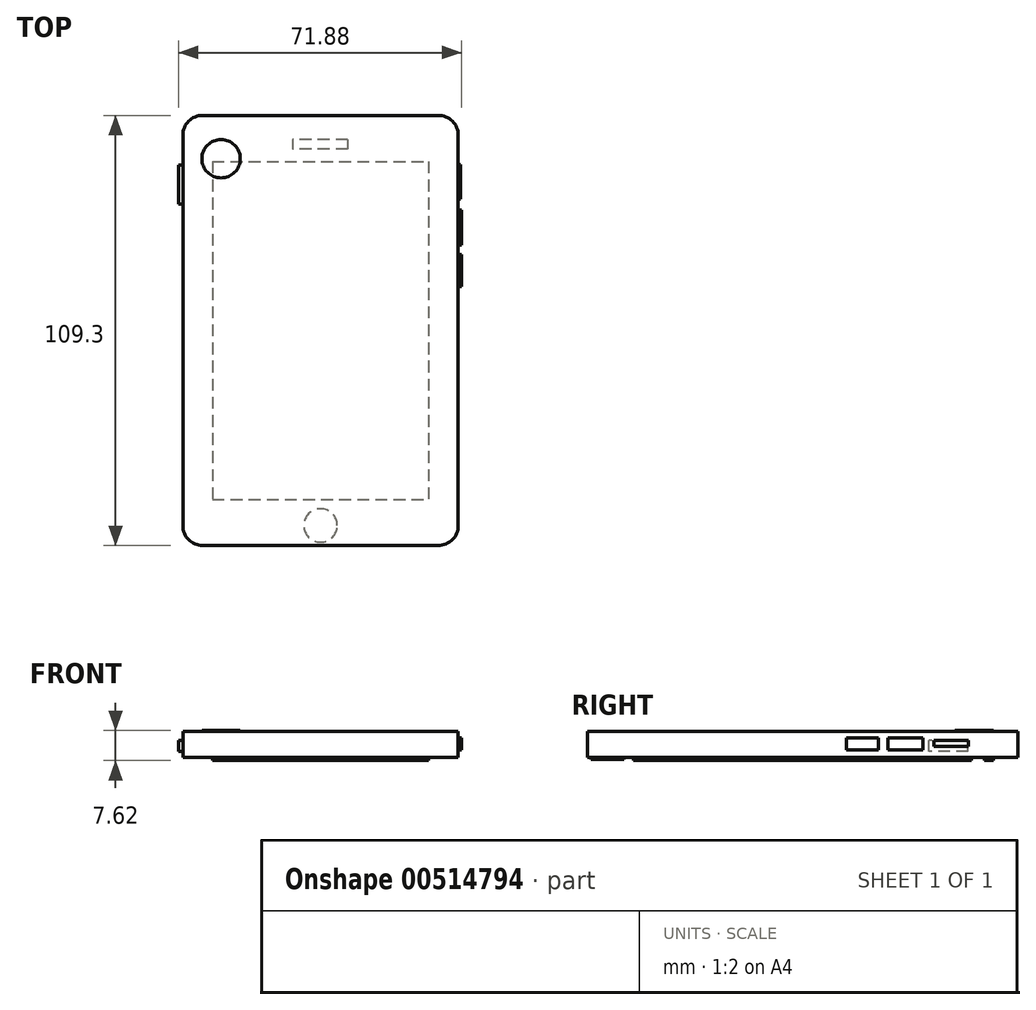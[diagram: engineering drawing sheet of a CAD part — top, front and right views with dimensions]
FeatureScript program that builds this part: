
annotation { "Feature Type Name" : "Feature", "Feature Type Description" : "" }
export const myFeature = defineFeature(function(context is Context, id is Id, definition is map)
    precondition{}
    {
        {
            var Q0;
            Q0=qCreatedBy(makeId("Top.planeOp"),FACE);
            var sketch = newSketch(context, id + "F0", { "sketchPlane" : qUnion([Q0])});
            skLineSegment(sketch, "E0.bottom", {"start": v(-30.02, 51.45) * mm, "end": v(30.02, 51.45) * mm});
            skLineSegment(sketch, "E0.top", {"start": v(-30.02, -51.45) * mm, "end": v(30.02, -51.45) * mm});
            skLineSegment(sketch, "E0.left", {"start": v(-30.02, 51.45) * mm, "end": v(-30.02, -51.45) * mm});
            skLineSegment(sketch, "E0.right", {"start": v(30.02, 51.45) * mm, "end": v(30.02, -51.45) * mm});
            skPoint(sketch, "E0.middle", {"position": v(0, 0) * mm});
            skLineSegment(sketch, "E1.bottom", {"start": v(-34.98, 54.65) * mm, "end": v(34.98, 54.65) * mm});
            skLineSegment(sketch, "E1.top", {"start": v(-34.98, -54.65) * mm, "end": v(34.98, -54.65) * mm});
            skLineSegment(sketch, "E1.left", {"start": v(-34.98, 54.65) * mm, "end": v(-34.98, -54.65) * mm});
            skLineSegment(sketch, "E1.right", {"start": v(34.98, 54.65) * mm, "end": v(34.98, -54.65) * mm});
            skSolve(sketch);
        }
        {
            var Q0;
            Q0=makeQuery(id+"F0.imprint","IMPRINT",FACE,{"disambiguationData":[TD([[makeQuery(id+"F0.imprint","IMPRINT",EDGE,{"derivedFrom":sQuery(id+"F0.wireOp",EDGE,"E0.bottom")}),-1.0]])]});
            var Q1;
            Q1=makeQuery(id+"F0.imprint","IMPRINT",FACE,{"disambiguationData":[TD([[makeQuery(id+"F0.imprint","IMPRINT",EDGE,{"derivedFrom":sQuery(id+"F0.wireOp",EDGE,"E0.bottom")}),1.0]])]});
            extrude(context, id + "F1", {"entities" : qUnion([Q0, Q1]), "depth" : 6.6 * mm, "offsetDistance" : 25.4 * mm});
        }
        {
            var Q0;
            Q0=makeQuery(id+"F1.opExtrude","SWEPT_EDGE",EDGE,{"disambiguationData":[OSD([sQuery(id+"F0.wireOp",EDGE,"E1.top"),sQuery(id+"F0.wireOp",EDGE,"E1.right")])]});
            fillet(context, id + "F2", {"entities" : qUnion([Q0]), "radius" : 5.08 * mm, "tangentPropagation" : true, "allowEdgeOverflow" : false});
        }
        {
            var Q0;
            Q0=makeQuery(id+"F1.opExtrude","SWEPT_EDGE",EDGE,{"disambiguationData":[OSD([sQuery(id+"F0.wireOp",EDGE,"E1.top"),sQuery(id+"F0.wireOp",EDGE,"E1.left")])]});
            fillet(context, id + "F3", {"entities" : qUnion([Q0]), "radius" : 5.08 * mm, "tangentPropagation" : true, "allowEdgeOverflow" : false});
        }
        {
            var Q0;
            Q0=makeQuery(id+"F1.opExtrude","SWEPT_EDGE",EDGE,{"disambiguationData":[OSD([sQuery(id+"F0.wireOp",EDGE,"E1.bottom"),sQuery(id+"F0.wireOp",EDGE,"E1.right")])]});
            fillet(context, id + "F4", {"entities" : qUnion([Q0]), "radius" : 5.08 * mm, "tangentPropagation" : true, "allowEdgeOverflow" : false});
        }
        {
            var Q0;
            Q0=makeQuery(id+"F1.opExtrude","SWEPT_EDGE",EDGE,{"disambiguationData":[OSD([sQuery(id+"F0.wireOp",EDGE,"E1.bottom"),sQuery(id+"F0.wireOp",EDGE,"E1.left")])]});
            fillet(context, id + "F5", {"entities" : qUnion([Q0]), "radius" : 5.08 * mm, "tangentPropagation" : true, "allowEdgeOverflow" : false});
        }
        {
            var Q0;
            Q0=qCreatedBy(makeId("Top.planeOp"),FACE);
            var sketch = newSketch(context, id + "F6", { "sketchPlane" : qUnion([Q0])});
            skLineSegment(sketch, "E2.bottom", {"start": v(-27.45, 42.93) * mm, "end": v(27.45, 42.93) * mm});
            skLineSegment(sketch, "E2.top", {"start": v(-27.45, -42.93) * mm, "end": v(27.45, -42.93) * mm});
            skLineSegment(sketch, "E2.left", {"start": v(-27.45, 42.93) * mm, "end": v(-27.45, -42.93) * mm});
            skLineSegment(sketch, "E2.right", {"start": v(27.45, 42.93) * mm, "end": v(27.45, -42.93) * mm});
            skPoint(sketch, "E2.middle", {"position": v(0, 0) * mm});
            skSolve(sketch);
        }
        {
            var Q0;
            Q0=qCreatedBy(makeId("Top.planeOp"),FACE);
            var sketch = newSketch(context, id + "F7", { "sketchPlane" : qUnion([Q0])});
            skCircle(sketch, "E3", {"center": v(0, -49.1) * mm, "radius": 4.54 * mm});
            skSolve(sketch);
        }
        {
            var Q0;
            Q0=makeQuery(id+"F7.imprint","IMPRINT",FACE,{"disambiguationData":[TD([[makeQuery(id+"F7.imprint","IMPRINT",EDGE,{"derivedFrom":sQuery(id+"F7.wireOp",EDGE,"E3")}),1.0]])]});
            extrude(context, id + "F8", {"entities" : qUnion([Q0]), "operationType" : NewBodyOperationType.ADD, "depth" : 5.08 * mm, "offsetDistance" : 25.4 * mm});
        }
        {
            var Q0;
            Q0=qCreatedBy(makeId("Top.planeOp"),FACE);
            var sketch = newSketch(context, id + "F9", { "sketchPlane" : qUnion([Q0])});
            skCircle(sketch, "E4", {"center": v(0, -49.55) * mm, "radius": 4.25 * mm});
            skSolve(sketch);
        }
        {
            var Q0;
            Q0=makeQuery(id+"F6.imprint","IMPRINT",FACE,{"disambiguationData":[TD([[makeQuery(id+"F6.imprint","IMPRINT",EDGE,{"derivedFrom":sQuery(id+"F6.wireOp",EDGE,"E2.bottom")}),-1.0]])]});
            extrude(context, id + "F10", {"entities" : qUnion([Q0]), "operationType" : NewBodyOperationType.ADD, "oppositeDirection" : true, "depth" : 0.76 * mm, "offsetDistance" : 25.4 * mm});
        }
        {
            var Q0;
            Q0=makeQuery(id+"F9.imprint","IMPRINT",FACE,{"disambiguationData":[TD([[makeQuery(id+"F9.imprint","IMPRINT",EDGE,{"derivedFrom":sQuery(id+"F9.wireOp",EDGE,"E4")}),1.0]])]});
            extrude(context, id + "F11", {"entities" : qUnion([Q0]), "operationType" : NewBodyOperationType.ADD, "oppositeDirection" : true, "depth" : 0.5 * mm, "offsetDistance" : 25.4 * mm});
        }
        {
            var Q0;
            Q0=qCreatedBy(makeId("Right.planeOp"),FACE);
            var sketch = newSketch(context, id + "F12", { "sketchPlane" : qUnion([Q0])});
            skLineSegment(sketch, "E5.bottom", {"start": v(43.51, 1.78) * mm, "end": v(31.55, 1.78) * mm});
            skLineSegment(sketch, "E5.top", {"start": v(43.51, 4.92) * mm, "end": v(31.55, 4.92) * mm});
            skLineSegment(sketch, "E5.left", {"start": v(43.51, 1.78) * mm, "end": v(43.51, 4.92) * mm});
            skLineSegment(sketch, "E5.right", {"start": v(31.55, 1.78) * mm, "end": v(31.55, 4.92) * mm});
            skSolve(sketch);
        }
        {
            var Q0;
            Q0=makeQuery(id+"F12.imprint","IMPRINT",FACE,{"disambiguationData":[TD([[makeQuery(id+"F12.imprint","IMPRINT",EDGE,{"derivedFrom":sQuery(id+"F12.wireOp",EDGE,"E5.bottom")}),-1.0]])]});
            extrude(context, id + "F13", {"entities" : qUnion([Q0]), "operationType" : NewBodyOperationType.ADD, "depth" : 27.43 * mm, "offsetDistance" : 25.4 * mm});
        }
        {
            var Q0;
            Q0=qCreatedBy(makeId("Right.planeOp"),FACE);
            var sketch = newSketch(context, id + "F14", { "sketchPlane" : qUnion([Q0])});
            skLineSegment(sketch, "E6.bottom", {"start": v(42.06, 1.53) * mm, "end": v(32.16, 1.53) * mm});
            skLineSegment(sketch, "E6.top", {"start": v(42.06, 4.4) * mm, "end": v(32.16, 4.4) * mm});
            skLineSegment(sketch, "E6.left", {"start": v(42.06, 1.53) * mm, "end": v(42.06, 4.4) * mm});
            skLineSegment(sketch, "E6.right", {"start": v(32.16, 1.53) * mm, "end": v(32.16, 4.4) * mm});
            skSolve(sketch);
        }
        {
            var Q0;
            Q0=makeQuery(id+"F14.imprint","IMPRINT",FACE,{"disambiguationData":[TD([[makeQuery(id+"F14.imprint","IMPRINT",EDGE,{"derivedFrom":sQuery(id+"F14.wireOp",EDGE,"E6.bottom")}),-1.0]])]});
            extrude(context, id + "F15", {"entities" : qUnion([Q0]), "operationType" : NewBodyOperationType.ADD, "oppositeDirection" : true, "depth" : 36.07 * mm, "offsetDistance" : 25.4 * mm});
        }
        {
            var Q0;
            Q0=qCreatedBy(makeId("Right.planeOp"),FACE);
            var sketch = newSketch(context, id + "F16", { "sketchPlane" : qUnion([Q0])});
            skLineSegment(sketch, "E7.bottom", {"start": v(42.1, 4.32) * mm, "end": v(33.36, 4.32) * mm});
            skLineSegment(sketch, "E7.top", {"start": v(42.1, 2.78) * mm, "end": v(33.36, 2.78) * mm});
            skLineSegment(sketch, "E7.left", {"start": v(42.1, 4.32) * mm, "end": v(42.1, 2.78) * mm});
            skLineSegment(sketch, "E7.right", {"start": v(33.36, 4.32) * mm, "end": v(33.36, 2.78) * mm});
            skSolve(sketch);
        }
        {
            var Q0;
            Q0=makeQuery(id+"F16.imprint","IMPRINT",FACE,{"disambiguationData":[TD([[makeQuery(id+"F16.imprint","IMPRINT",EDGE,{"derivedFrom":sQuery(id+"F16.wireOp",EDGE,"E7.bottom")}),1.0]])]});
            extrude(context, id + "F17", {"entities" : qUnion([Q0]), "operationType" : NewBodyOperationType.ADD, "depth" : 35.56 * mm, "offsetDistance" : 25.4 * mm});
        }
        {
            var Q0;
            Q0=qCreatedBy(makeId("Right.planeOp"),FACE);
            var sketch = newSketch(context, id + "F18", { "sketchPlane" : qUnion([Q0])});
            skLineSegment(sketch, "E8.bottom", {"start": v(30.55, 4.97) * mm, "end": v(21.68, 4.97) * mm});
            skLineSegment(sketch, "E8.top", {"start": v(30.55, 1.97) * mm, "end": v(21.68, 1.97) * mm});
            skLineSegment(sketch, "E8.left", {"start": v(30.55, 4.97) * mm, "end": v(30.55, 1.97) * mm});
            skLineSegment(sketch, "E8.right", {"start": v(21.68, 4.97) * mm, "end": v(21.68, 1.97) * mm});
            skSolve(sketch);
        }
        {
            var Q0;
            Q0=qCreatedBy(makeId("Right.planeOp"),FACE);
            var sketch = newSketch(context, id + "F19", { "sketchPlane" : qUnion([Q0])});
            skLineSegment(sketch, "E9.bottom", {"start": v(19.3, 4.97) * mm, "end": v(11.18, 4.97) * mm});
            skLineSegment(sketch, "E9.top", {"start": v(19.3, 1.97) * mm, "end": v(11.18, 1.97) * mm});
            skLineSegment(sketch, "E9.left", {"start": v(19.3, 4.97) * mm, "end": v(19.3, 1.97) * mm});
            skLineSegment(sketch, "E9.right", {"start": v(11.18, 4.97) * mm, "end": v(11.18, 1.97) * mm});
            skSolve(sketch);
        }
        {
            var Q0;
            Q0=makeQuery(id+"F18.imprint","IMPRINT",FACE,{"disambiguationData":[TD([[makeQuery(id+"F18.imprint","IMPRINT",EDGE,{"derivedFrom":sQuery(id+"F18.wireOp",EDGE,"E8.bottom")}),1.0]])]});
            extrude(context, id + "F20", {"entities" : qUnion([Q0]), "operationType" : NewBodyOperationType.ADD, "depth" : 35.81 * mm, "offsetDistance" : 25.4 * mm});
        }
        {
            var Q0;
            Q0=makeQuery(id+"F19.imprint","IMPRINT",FACE,{"disambiguationData":[TD([[makeQuery(id+"F19.imprint","IMPRINT",EDGE,{"derivedFrom":sQuery(id+"F19.wireOp",EDGE,"E9.bottom")}),1.0]])]});
            extrude(context, id + "F21", {"entities" : qUnion([Q0]), "operationType" : NewBodyOperationType.ADD, "depth" : 35.81 * mm, "offsetDistance" : 25.4 * mm});
        }
        {
            var Q0;
            Q0=qCreatedBy(makeId("Front.planeOp"),FACE);
            var sketch = newSketch(context, id + "F22", { "sketchPlane" : qUnion([Q0])});
            skLineSegment(sketch, "E10.bottom", {"start": v(3.3, 3) * mm, "end": v(-3.9, 3) * mm});
            skLineSegment(sketch, "E10.top", {"start": v(3.3, 4.43) * mm, "end": v(-3.9, 4.43) * mm});
            skLineSegment(sketch, "E10.left", {"start": v(3.3, 3) * mm, "end": v(3.3, 4.43) * mm});
            skLineSegment(sketch, "E10.right", {"start": v(-3.9, 3) * mm, "end": v(-3.9, 4.43) * mm});
            skSolve(sketch);
        }
        {
            var Q0;
            Q0=makeQuery(id+"F22.imprint","IMPRINT",FACE,{"disambiguationData":[TD([[makeQuery(id+"F22.imprint","IMPRINT",EDGE,{"derivedFrom":sQuery(id+"F22.wireOp",EDGE,"E10.bottom")}),-1.0]])]});
            extrude(context, id + "F23", {"entities" : qUnion([Q0]), "operationType" : NewBodyOperationType.ADD, "depth" : 54.6 * mm, "offsetDistance" : 25.4 * mm});
        }
        {
            var Q0;
            Q0=qCreatedBy(makeId("Top.planeOp"),FACE);
            var sketch = newSketch(context, id + "F24", { "sketchPlane" : qUnion([Q0])});
            skCircle(sketch, "E11", {"center": v(-25.26, 43.64) * mm, "radius": 4.88 * mm});
            skSolve(sketch);
        }
        {
            var Q0;
            Q0=makeQuery(id+"F24.imprint","IMPRINT",FACE,{"disambiguationData":[TD([[makeQuery(id+"F24.imprint","IMPRINT",EDGE,{"derivedFrom":sQuery(id+"F24.wireOp",EDGE,"E11")}),1.0]])]});
            extrude(context, id + "F25", {"entities" : qUnion([Q0]), "operationType" : NewBodyOperationType.ADD, "depth" : 6.86 * mm, "offsetDistance" : 25.4 * mm});
        }
        {
            var Q0;
            Q0=qCreatedBy(makeId("Top.planeOp"),FACE);
            var sketch = newSketch(context, id + "F26", { "sketchPlane" : qUnion([Q0])});
            skLineSegment(sketch, "E12.bottom", {"start": v(6.89, 48.45) * mm, "end": v(-7.08, 48.45) * mm});
            skLineSegment(sketch, "E12.top", {"start": v(6.89, 46.15) * mm, "end": v(-7.08, 46.15) * mm});
            skLineSegment(sketch, "E12.left", {"start": v(6.89, 48.45) * mm, "end": v(6.89, 46.15) * mm});
            skLineSegment(sketch, "E12.right", {"start": v(-7.08, 48.45) * mm, "end": v(-7.08, 46.15) * mm});
            skSolve(sketch);
        }
        {
            var Q0;
            Q0=makeQuery(id+"F26.imprint","IMPRINT",FACE,{"disambiguationData":[TD([[makeQuery(id+"F26.imprint","IMPRINT",EDGE,{"derivedFrom":sQuery(id+"F26.wireOp",EDGE,"E12.bottom")}),1.0]])]});
            extrude(context, id + "F27", {"entities" : qUnion([Q0]), "operationType" : NewBodyOperationType.ADD, "oppositeDirection" : true, "depth" : 0.76 * mm, "offsetDistance" : 25.4 * mm});
        }
    });
